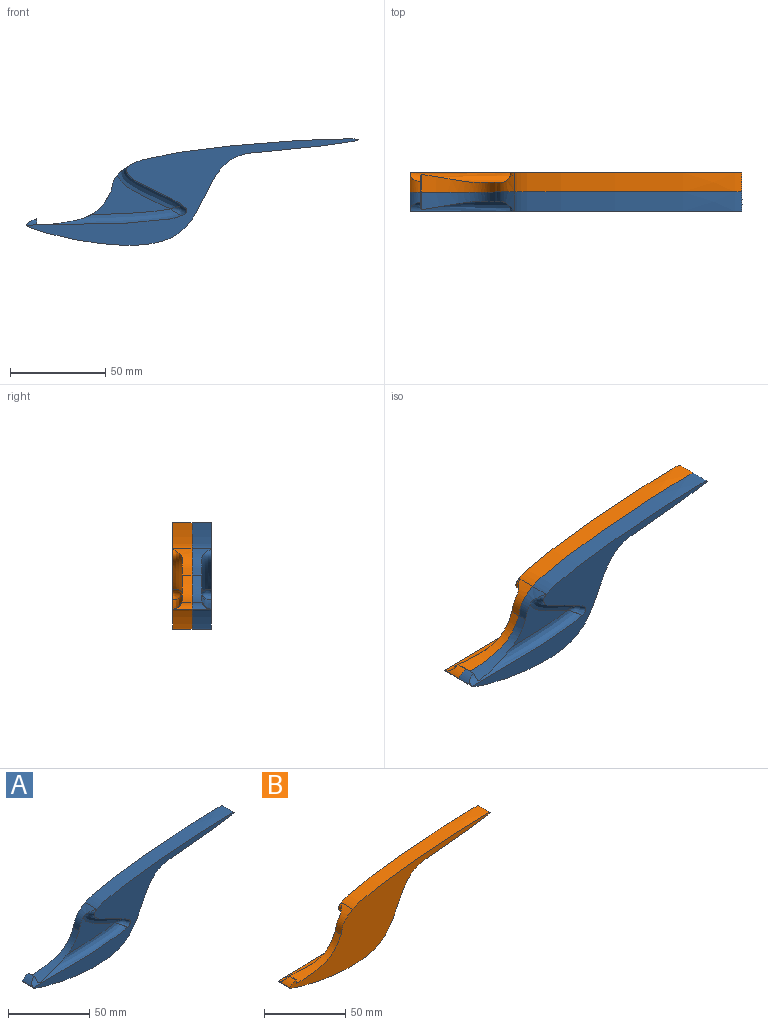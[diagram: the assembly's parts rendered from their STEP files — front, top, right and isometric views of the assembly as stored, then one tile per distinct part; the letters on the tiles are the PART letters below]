
ASSEMBLY  parts=2 mates=1
PART A: 14 faces, bbox 212.4x15.8x72.4 mm
  f0: extruded ~119.18x13.66mm, area 1796.2mm2, adj f1,f2,f3,f4
  f1: extruded ~118.45x48.38mm, area 1445.3mm2, adj f0,f2,f3,f7
  f2: plane 212.32x72.35mm, normal (0,-1,0), area 2065.6mm2, adj f0,f1,f9,f10,f11
  f3: plane 204.55x66.73mm, normal (0,1,0), area 2902.7mm2, adj f0,f1,f4,f5,f6,f7,f12,f13
  f4: extruded ~13.82x10.22mm, area 115.7mm2, adj f0,f3,f5,f8,f9
  f5: extruded ~38.52x17.74mm, area 284.8mm2, adj f3,f4,f8,f11,f12
  f6: plane 8.01x2.58mm, normal (1,0,0), area 16.5mm2, adj f3,f11,f12,f13
  f7: cylinder r=12.49mm len=10.16mm, axis (0,-1,0), area 49.7mm2, adj f1,f3,f11,f13
  f8: plane 41.91x21.52mm, normal (0,-1,0), area 347.2mm2, adj f4,f5,f9,f11
  f9: bspline ~34.82x30.15mm, area 288mm2, adj f2,f4,f8,f10
  f10: bspline ~8.62x5.6mm, area 32.8mm2, adj f2,f9,f11
  f11: bspline ~85.1x9.6mm, area 493.7mm2, adj f2,f5,f6,f7,f8,f10,f12,f13
  f12: cylinder r=0.41mm len=9.27mm, axis (0,-1,0), area 5.7mm2, adj f3,f5,f6,f11
  f13: cylinder r=0.2mm len=5.5mm, axis (0,-1,0), area 2mm2, adj f3,f6,f7,f11
PART B: 14 faces, bbox 212.4x15.8x72.4 mm
  f0: extruded ~119.18x13.66mm, area 1796.2mm2, adj f1,f2,f3,f4
  f1: extruded ~118.45x48.38mm, area 1445.3mm2, adj f0,f2,f3,f7
  f2: plane 204.55x66.73mm, normal (0,-1,0), area 2902.7mm2, adj f0,f1,f4,f5,f6,f7,f12,f13
  f3: plane 212.34x72.37mm, normal (0,1,0), area 2065.6mm2, adj f0,f1,f9,f10,f11
  f4: extruded ~13.82x10.22mm, area 115.7mm2, adj f0,f2,f5,f8,f9
  f5: extruded ~38.52x17.74mm, area 284.8mm2, adj f2,f4,f8,f11,f12
  f6: plane 8.01x2.58mm, normal (1,0,0), area 16.5mm2, adj f2,f11,f12,f13
  f7: cylinder r=12.49mm len=10.16mm, axis (0,1,0), area 49.7mm2, adj f1,f2,f11,f13
  f8: plane 41.91x21.52mm, normal (0,1,0), area 347.2mm2, adj f4,f5,f9,f11
  f9: bspline ~35.55x30.66mm, area 288mm2, adj f3,f4,f8,f10
  f10: bspline ~8.62x5.58mm, area 32.5mm2, adj f3,f9,f11
  f11: bspline ~84.9x9.55mm, area 493.7mm2, adj f3,f5,f6,f7,f8,f10,f12,f13
  f12: cylinder r=0.41mm len=9.27mm, axis (0,1,0), area 5.7mm2, adj f2,f5,f6,f11
  f13: cylinder r=0.2mm len=5.5mm, axis (0,1,0), area 2mm2, adj f2,f6,f7,f11
PLACE A t=(5.52,-1.3,-21.67)mm
PLACE B t=(5.52,8.86,-21.67)mm
MATE fastened A.f3 <-> B.f2  axis (0,1,0) through (-16.38,3.78,-6.03)mm
